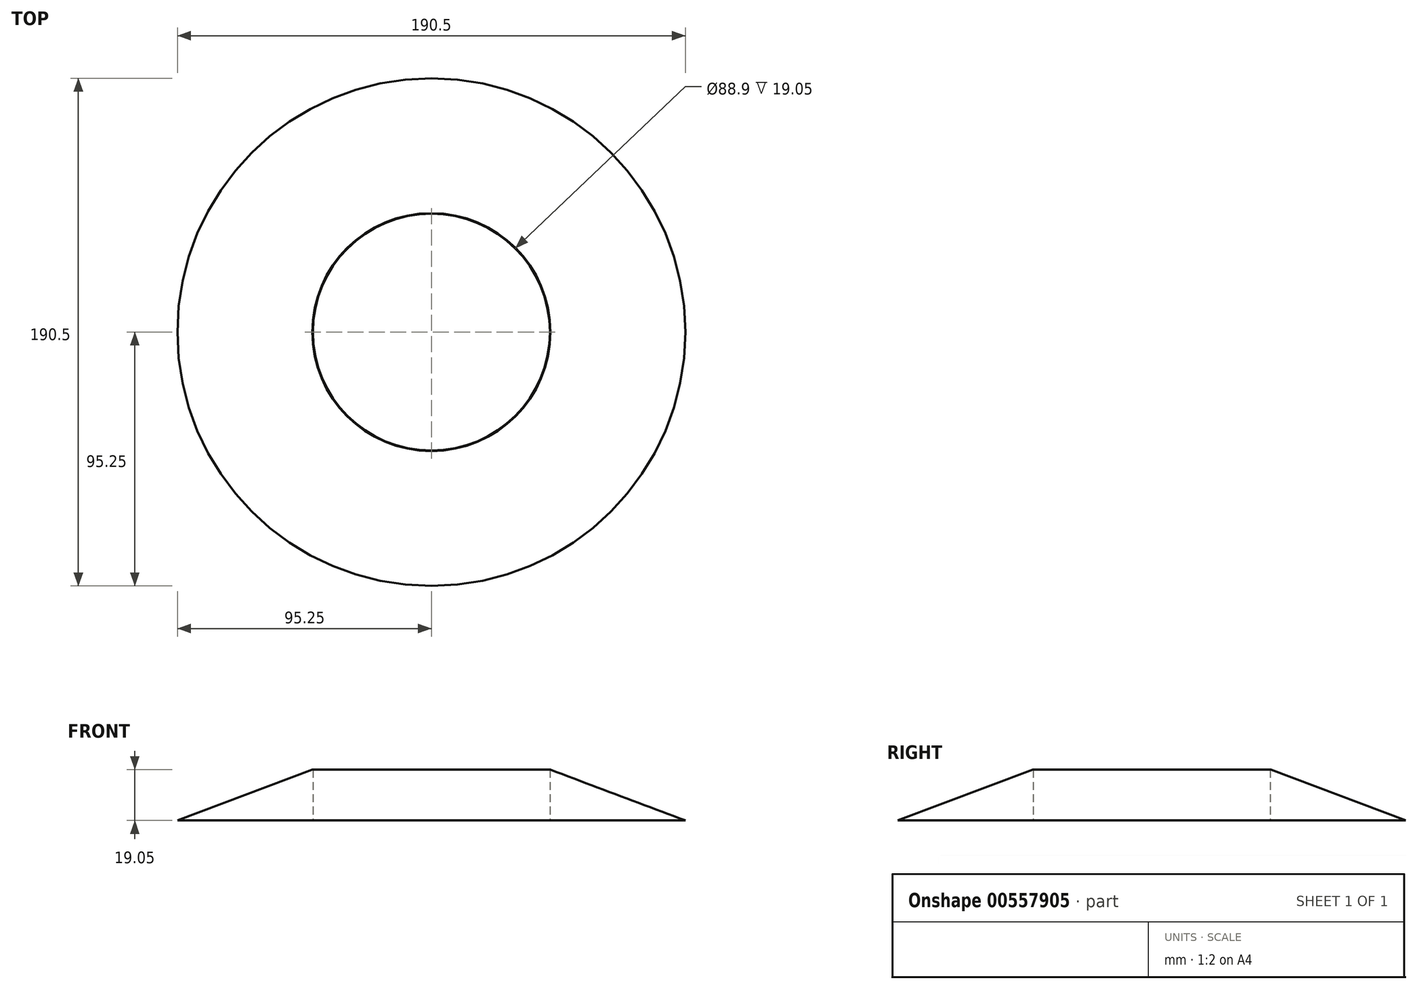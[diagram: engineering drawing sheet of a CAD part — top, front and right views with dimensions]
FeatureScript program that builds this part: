
annotation { "Feature Type Name" : "Feature", "Feature Type Description" : "" }
export const myFeature = defineFeature(function(context is Context, id is Id, definition is map)
    precondition{}
    {
        {
            var Q0;
            Q0=qCreatedBy(makeId("Top.planeOp"),FACE);
            var sketch = newSketch(context, id + "F0", { "sketchPlane" : qUnion([Q0])});
            skCircle(sketch, "E0", {"center": v(0, 0) * mm, "radius": 95.25 * mm});
            skCircle(sketch, "E1", {"center": v(0, 0) * mm, "radius": 44.45 * mm});
            skSolve(sketch);
        }
        {
            var Q0;
            Q0=makeQuery(id+"F0.imprint","IMPRINT",FACE,{"disambiguationData":[TD([[makeQuery(id+"F0.imprint","IMPRINT",EDGE,{"derivedFrom":sQuery(id+"F0.wireOp",EDGE,"E0")}),1.0]])]});
            extrude(context, id + "F1", {"entities" : qUnion([Q0]), "depth" : 19.05 * mm, "offsetDistance" : 25.4 * mm});
        }
        {
            var Q0;
            Q0=qCreatedBy(makeId("Front.planeOp"),FACE);
            var sketch = newSketch(context, id + "F2", { "sketchPlane" : qUnion([Q0])});
            skLineSegment(sketch, "E2", {"start": v(-44.41, 19.14) * mm, "end": v(-95.25, 0) * mm});
            skLineSegment(sketch, "E3", {"start": v(-95.25, 0) * mm, "end": v(-107.2, 21.62) * mm});
            skLineSegment(sketch, "E4", {"start": v(-107.2, 21.62) * mm, "end": v(-52.87, 28.86) * mm});
            skLineSegment(sketch, "E5", {"start": v(-52.87, 28.86) * mm, "end": v(-44.41, 19.14) * mm});
            skSolve(sketch);
        }
        {
            var Q0;
            Q0=makeQuery(id+"F2.imprint","IMPRINT",FACE,{"disambiguationData":[TD([[makeQuery(id+"F2.imprint","IMPRINT",EDGE,{"derivedFrom":sQuery(id+"F2.wireOp",EDGE,"E2")}),-1.0]])]});
            var Q1;
            Q1=makeQuery(id+"F1.opExtrude","CAP_EDGE",EDGE,{"disambiguationData":[OSD([sQuery(id+"F0.wireOp",EDGE,"E1")])],"isStart":true});
            revolve(context, id + "F3", {"operationType" : NewBodyOperationType.REMOVE, "entities" : qUnion([Q0]), "axis" : qUnion([Q1]), "revolveType" : RevolveType.FULL, "oppositeDirection" : true});
        }
    });
